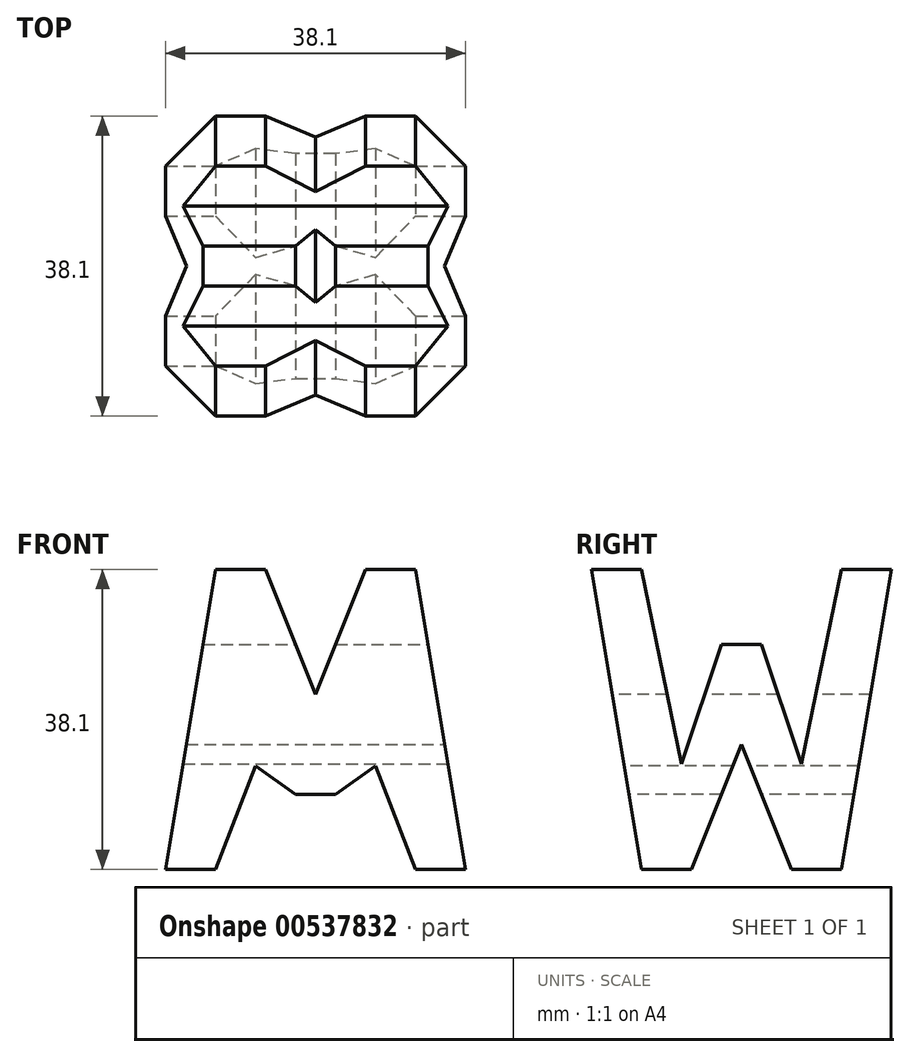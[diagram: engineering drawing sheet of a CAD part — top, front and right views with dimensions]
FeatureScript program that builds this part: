
annotation { "Feature Type Name" : "Feature", "Feature Type Description" : "" }
export const myFeature = defineFeature(function(context is Context, id is Id, definition is map)
    precondition{}
    {
        {
            var Q0;
            Q0=qCreatedBy(makeId("Front.planeOp"),FACE);
            var sketch = newSketch(context, id + "F0", { "sketchPlane" : qUnion([Q0])});
            skLineSegment(sketch, "E0", {"start": v(0, 0) * mm, "end": v(0, 38.1) * mm});
            skLineSegment(sketch, "E1", {"start": v(0, 0) * mm, "end": v(38.1, 0) * mm});
            skLineSegment(sketch, "E2", {"start": v(38.1, 0) * mm, "end": v(38.1, 38.1) * mm});
            skLineSegment(sketch, "E3", {"start": v(38.1, 38.1) * mm, "end": v(0, 38.1) * mm});
            skSolve(sketch);
        }
        {
            var Q0;
            Q0=makeQuery(id+"F0.imprint","IMPRINT",FACE,{"disambiguationData":[TD([[makeQuery(id+"F0.imprint","IMPRINT",EDGE,{"derivedFrom":sQuery(id+"F0.wireOp",EDGE,"E0")}),-1.0]])]});
            extrude(context, id + "F1", {"entities" : qUnion([Q0]), "depth" : 38.1 * mm, "offsetDistance" : 25.4 * mm});
        }
        {
            var Q0;
            Q0=qCreatedBy(makeId("Front.planeOp"),FACE);
            cPlane(context, id + "F2", {"entities" : qUnion([Q0]), "cplaneType" : CPlaneType.OFFSET, "offset" : 38.1 * mm, "width" : 152.4 * mm, "height" : 152.4 * mm});
        }
        {
            var Q0;
            Q0=qCreatedBy(makeId("Right.planeOp"),FACE);
            cPlane(context, id + "F3", {"entities" : qUnion([Q0]), "cplaneType" : CPlaneType.OFFSET, "offset" : 38.1 * mm, "width" : 152.4 * mm, "height" : 152.4 * mm});
        }
        {
            var Q0;
            Q0=qCreatedBy(id+"F3.planeOp",FACE);
            var sketch = newSketch(context, id + "F4", { "sketchPlane" : qUnion([Q0])});
            skLineSegment(sketch, "E4", {"start": v(-38.1, 38.1) * mm, "end": v(-38.1, 0) * mm});
            skLineSegment(sketch, "E5", {"start": v(0, 0) * mm, "end": v(-38.1, 0) * mm});
            skLineSegment(sketch, "E6", {"start": v(0, 38.1) * mm, "end": v(-38.1, 38.1) * mm});
            skLineSegment(sketch, "E7", {"start": v(-38.1, 38.1) * mm, "end": v(-31.75, 0) * mm});
            skLineSegment(sketch, "E8", {"start": v(-31.75, 0) * mm, "end": v(-25.4, 0) * mm});
            skLineSegment(sketch, "E9", {"start": v(-25.4, 0) * mm, "end": v(-19.05, 15.87) * mm});
            skLineSegment(sketch, "E10", {"start": v(-19.05, 15.87) * mm, "end": v(-12.7, 0) * mm});
            skLineSegment(sketch, "E11", {"start": v(-12.7, 0) * mm, "end": v(-6.35, 0) * mm});
            skLineSegment(sketch, "E12", {"start": v(-6.35, 0) * mm, "end": v(0, 38.1) * mm});
            skLineSegment(sketch, "E13", {"start": v(0, 38.1) * mm, "end": v(-6.35, 38.1) * mm});
            skLineSegment(sketch, "E14", {"start": v(-6.35, 38.1) * mm, "end": v(-11.43, 13.4) * mm});
            skLineSegment(sketch, "E15", {"start": v(-26.67, 13.4) * mm, "end": v(-31.75, 38.1) * mm});
            skLineSegment(sketch, "E16", {"start": v(-26.67, 13.4) * mm, "end": v(-21.59, 28.57) * mm});
            skLineSegment(sketch, "E17", {"start": v(-21.6, 28.57) * mm, "end": v(-16.51, 28.57) * mm});
            skLineSegment(sketch, "E18", {"start": v(-16.5, 28.58) * mm, "end": v(-11.43, 13.4) * mm});
            skLineSegment(sketch, "E19", {"start": v(0, 0) * mm, "end": v(0, 38.1) * mm});
            skSolve(sketch);
        }
        {
            var Q0;
            {var subQ1=sQuery(id+"F4.wireOp",EDGE,"E14");Q0=makeQuery(id+"F4.imprint","IMPRINT",FACE,{"disambiguationData":[TD([[makeQuery(id+"F4.imprint","IMPRINT",EDGE,{"derivedFrom":subQ1}),-1.0]])]});}
            var Q1;
            {var subQ0=sQuery(id+"F4.wireOp",EDGE,"E9");Q1=makeQuery(id+"F4.imprint","IMPRINT",FACE,{"disambiguationData":[TD([[makeQuery(id+"F4.imprint","IMPRINT",EDGE,{"derivedFrom":subQ0}),-1.0]])]});}
            var Q2;
            {var subQ0=sQuery(id+"F4.wireOp",EDGE,"E4");Q2=makeQuery(id+"F4.imprint","IMPRINT",FACE,{"disambiguationData":[TD([[makeQuery(id+"F4.imprint","IMPRINT",EDGE,{"derivedFrom":subQ0}),1.0]])]});}
            var Q3;
            {var subQ2=sQuery(id+"F4.wireOp",EDGE,"E12");Q3=makeQuery(id+"F4.imprint","IMPRINT",FACE,{"disambiguationData":[TD([[makeQuery(id+"F4.imprint","IMPRINT",EDGE,{"derivedFrom":subQ2}),-1.0]])]});}
            extrude(context, id + "F5", {"entities" : qUnion([Q0, Q1, Q2, Q3]), "operationType" : NewBodyOperationType.REMOVE, "oppositeDirection" : true, "depth" : 38.1 * mm, "offsetDistance" : 25.4 * mm});
        }
        {
            var Q0;
            Q0=qCreatedBy(id+"F2.planeOp",FACE);
            var sketch = newSketch(context, id + "F6", { "sketchPlane" : qUnion([Q0])});
            skLineSegment(sketch, "E20", {"start": v(0, 0) * mm, "end": v(6.35, 38.1) * mm});
            skLineSegment(sketch, "E21", {"start": v(0, 0) * mm, "end": v(6.35, 0) * mm});
            skLineSegment(sketch, "E22", {"start": v(6.35, 0) * mm, "end": v(11.43, 13.16) * mm});
            skLineSegment(sketch, "E23", {"start": v(11.43, 13.16) * mm, "end": v(16.51, 9.53) * mm});
            skLineSegment(sketch, "E24", {"start": v(16.51, 9.53) * mm, "end": v(21.6, 9.53) * mm});
            skLineSegment(sketch, "E25", {"start": v(21.6, 9.52) * mm, "end": v(26.67, 13.16) * mm});
            skLineSegment(sketch, "E26", {"start": v(38.1, 0) * mm, "end": v(31.75, 38.1) * mm});
            skLineSegment(sketch, "E27", {"start": v(26.67, 13.16) * mm, "end": v(31.75, 0) * mm});
            skLineSegment(sketch, "E28", {"start": v(31.75, 0) * mm, "end": v(38.1, 0) * mm});
            skLineSegment(sketch, "E29", {"start": v(6.35, 38.1) * mm, "end": v(12.7, 38.1) * mm});
            skLineSegment(sketch, "E30", {"start": v(12.7, 38.1) * mm, "end": v(19.05, 22.23) * mm});
            skLineSegment(sketch, "E31", {"start": v(19.05, 22.23) * mm, "end": v(25.4, 38.1) * mm});
            skLineSegment(sketch, "E32", {"start": v(25.4, 38.1) * mm, "end": v(31.75, 38.1) * mm});
            skLineSegment(sketch, "E33", {"start": v(0, 0) * mm, "end": v(0, 38.1) * mm});
            skLineSegment(sketch, "E34", {"start": v(0, 38.1) * mm, "end": v(38.1, 38.1) * mm});
            skPoint(sketch, "E34.endSnap0", {"position": v(9.53, 38.1) * mm});
            skLineSegment(sketch, "E35", {"start": v(38.1, 38.1) * mm, "end": v(38.1, 0) * mm});
            skLineSegment(sketch, "E36", {"start": v(0, 38.1) * mm, "end": v(0, 0) * mm});
            skLineSegment(sketch, "E37", {"start": v(0, 0) * mm, "end": v(38.1, 0) * mm});
            skSolve(sketch);
        }
        {
            var Q0;
            {var subQ0=sQuery(id+"F6.wireOp",EDGE,"E22");Q0=makeQuery(id+"F6.imprint","IMPRINT",FACE,{"disambiguationData":[TD([[makeQuery(id+"F6.imprint","IMPRINT",EDGE,{"derivedFrom":subQ0}),-1.0]])]});}
            var Q1;
            {var subQ0=sQuery(id+"F6.wireOp",EDGE,"E30");Q1=makeQuery(id+"F6.imprint","IMPRINT",FACE,{"disambiguationData":[TD([[makeQuery(id+"F6.imprint","IMPRINT",EDGE,{"derivedFrom":subQ0}),1.0]])]});}
            var Q2;
            {var subQ0=sQuery(id+"F6.wireOp",EDGE,"E20");Q2=makeQuery(id+"F6.imprint","IMPRINT",FACE,{"disambiguationData":[TD([[makeQuery(id+"F6.imprint","IMPRINT",EDGE,{"derivedFrom":subQ0}),1.0]])]});}
            var Q3;
            {var subQ0=sQuery(id+"F6.wireOp",EDGE,"E26");Q3=makeQuery(id+"F6.imprint","IMPRINT",FACE,{"disambiguationData":[TD([[makeQuery(id+"F6.imprint","IMPRINT",EDGE,{"derivedFrom":subQ0}),-1.0]])]});}
            extrude(context, id + "F7", {"entities" : qUnion([Q0, Q1, Q2, Q3]), "operationType" : NewBodyOperationType.REMOVE, "oppositeDirection" : true, "depth" : 38.1 * mm, "offsetDistance" : 25.4 * mm});
        }
    });
